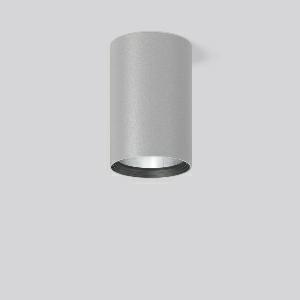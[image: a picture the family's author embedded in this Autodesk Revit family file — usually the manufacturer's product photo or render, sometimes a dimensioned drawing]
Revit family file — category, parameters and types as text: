
# Revit family: heledon_maxi_a_931246_004_2_7427
name_source: partatom
category: Lighting Fixtures
units: mm (PartAtom-declared; Revit-internal decimal feet)

## family parameters
Cut with Voids When Loaded = No
Host = Face
Light Source = No
Part Type = Normal
Room Calculation Point = No
Round Connector Dimension = Use Diameter
Shared = No

## types (1)
- HELEDON maxi A (1 x LED Modul 927 bakery, 3450 lm, 2700)
    Apparent Load = 33 VA
    Approval mark = CE
    CIE Flux Codes = 100 100 100 100 100
    Color Rendering = 90
    Color Temperature = 2700
    Default Elevation = 1800 mm
    Description = Series: HELEDON maxi
Cylindrical surface-mounted downlight. Housing: die-cast aluminium, powder-coated. Internal ceiling frame polycarbonate with bayonet mounting. Black plastic ring and recessed LED to prevent glare from the side. Optical assembly with reflector made of MIRO-Silver with 98% total light reflection for outstanding efficiency - can be changed without tools. Special LED for illumination of pastries included. Suitable for Ceiling mounting. Easy installation with a separate ceiling frame with bayonet mounting and plug connection. Driver integrated. Connected via plug-in connector. High quality converter without flickering and stroboscopic effect. The following accessories can be mounted without use of tools: interchangeable lenses, decorative glasses, honeycomb louvre, clear and frosted diffusers, white interchangeable plastic ring. 
Colour: silver
Diameter: 123 mm
Height: 183 mm
Lamp: LED
Socket: without socket
Colour temperature: bakery
Colour rendering index (CRI): 97
System power: 33 W
Rated luminous flux: 3450 lm
Luminous efficiency: 105 lm/W
Control gear: Regulated power supply
Protection class: I
Type of protection: IP 20
    Height = 183 mm
    Lamp = 1 x LED Modul 927 bakery
    Lamp Light Flux = 3450 lm
    Lamp count = 1
    Length = 123 mm
    Lifetime = 50000 h
    Luminous efficacy = 105 lm/W
    Manufacturer = RZB
    ModVariant = No
    Model = 931246.004.2
    Mounting Place = Ceiling
    Mounting Type = Surface mounted
    Number of Poles = 1
    OnlyDefault = Yes
    Power Factor = 1
    Product Name = HELEDON maxi A
    Product group = Surface mounted downlights
    ProductGroupID = 302
    Protection Class = Protection class I
    Protection Degree = IP 20
    RLX_Detail_Level = 1
    RLX_Emergency_Light_Flux = 0 lm
    RLX_Emergency_Type = 0
    RLX_Emergency_Type_DB = No
    RlxData = <blob elided: 97853 chars, md5=a483796c>
    Socket = socket
    Standby Power = 0 W
    System Light Flux = 3450 lm
    System Power = 33 W
    Type Comments = Product without accessories
    Type Image = 931192.004.jpg
    URL = http://relux.com
    VarID = ---
    Voltage = 230 V
    Voltage Range = 220-240 V
    Weight = 0.00 kg
    Width = 0 mm  [stored 0 ft]

note: [stored X ft] marks values corroborated as IEEE doubles in the binary element streams (Revit-internal decimal feet)

## geometry (parser evidence)
native form markers: Blend x4, Sweep x10
no freeform markers — native parametric forms only
